# Revit family: Toilet_Seat-U_Front-KOHLER-Escale-K-20192IN_1
name_source: partatom
category: Specialty Equipment
units: mm (PartAtom-declared; Revit-internal decimal feet)

## family parameters
Cut with Voids When Loaded = No
Host = Face
OmniClass Number = 23.31.25.00
Part Type = Normal
Room Calculation Point = No
Round Connector Dimension = Use Diameter
Shared = No

## types (4) — shared parameters
ADA Compliant = No
Assembly Code = C1030200
Date Modified = 9/17/2024
Default Elevation = 0"
Description = Quiet-Close toilet seat UF
Height = 1 15/16"
Length = 17 3/4"
Manufacturer = Kohler Co.
MasterFormat 2014 = 10820
MasterFormat 2014 Name = 10.28.13
Material = Vitreous China
Product Name = Escale
URL = https://www.kohler.co.in
WaterSense Certified = No
Width = 14 13/16"

## per-type parameters (varying)
| type | Finish | Model | Product Page URL | Type |
| 0-White | Kohler-Vitreous_China-0-White | K-2019IN-UF-0 | https://www.kohler.co.in | 1 |
| 7-Black Black | Kohler-Vitreous_China-7-Black_Black | K-2019IN-UF-7 | https://www.kohler.co.in | 2 |
| Antimicrobial, 0-White | Kohler-Vitreous_China-0-White | K-2019IN-SS-0 |  | 3 |
| Antimicrobial, 58-Thunder Grey | Kohler-Vitreous_China-58-Thunder_Grey | K-2019IN-SS-58 |  | 4 |

## geometry (parser evidence)
native form markers: Sweep x6
no freeform markers — native parametric forms only
